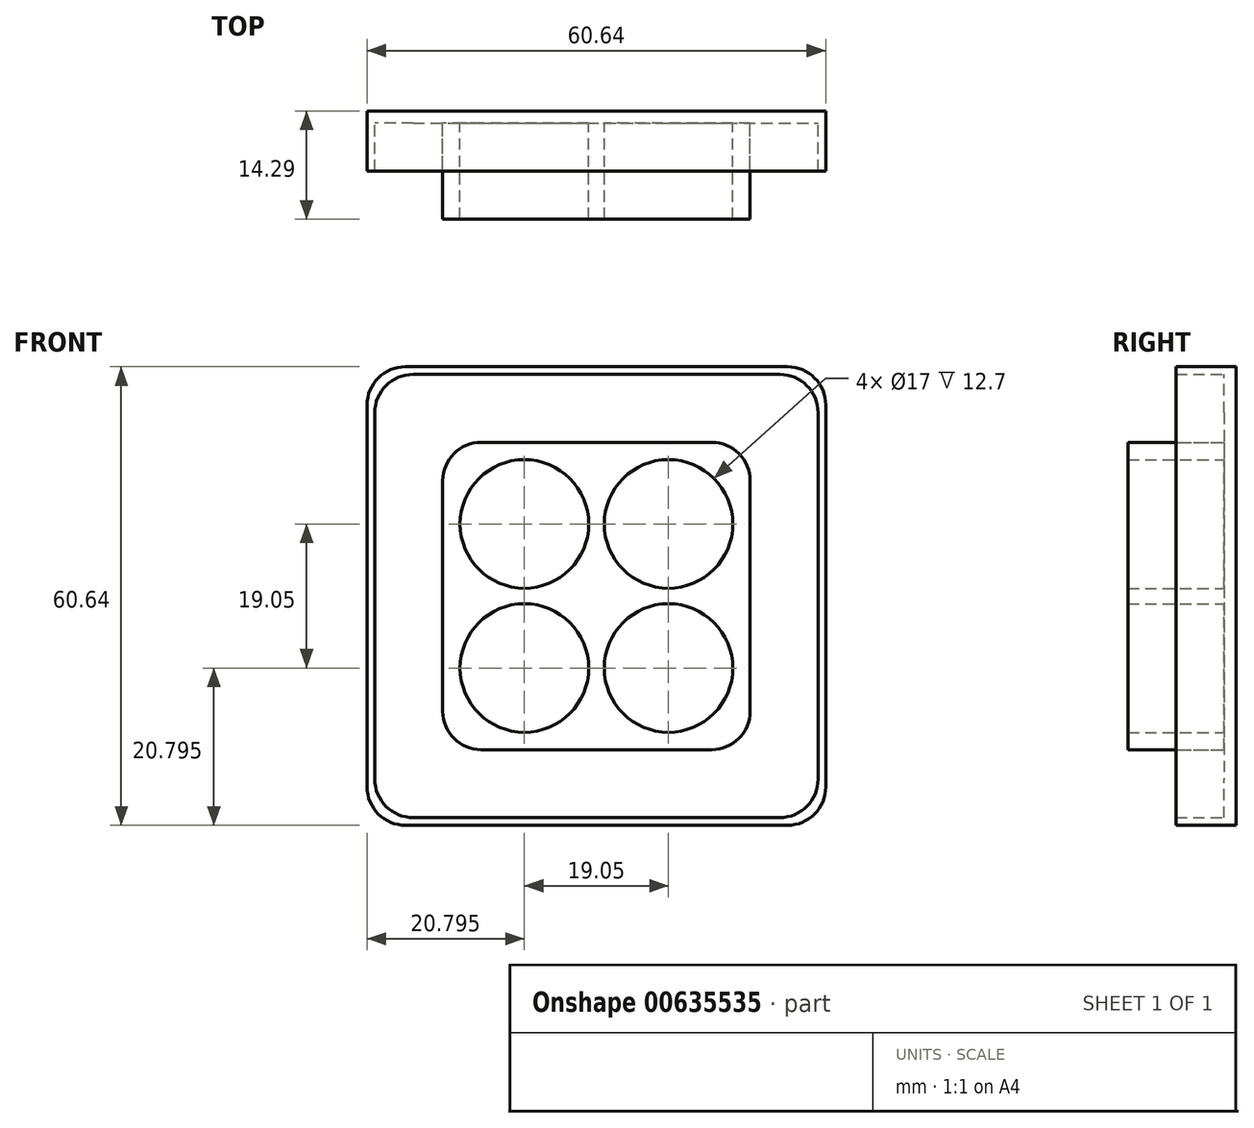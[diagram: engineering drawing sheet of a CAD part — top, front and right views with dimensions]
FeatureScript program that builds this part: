
annotation { "Feature Type Name" : "Feature", "Feature Type Description" : "" }
export const myFeature = defineFeature(function(context is Context, id is Id, definition is map)
    precondition{}
    {
        {
            var Q0;
            Q0=qCreatedBy(makeId("Front.planeOp"),FACE);
            var sketch = newSketch(context, id + "F0", { "sketchPlane" : qUnion([Q0])});
            skLineSegment(sketch, "E0.bottom", {"start": v(-35.56, 40.64) * mm, "end": v(-5.08, 40.64) * mm});
            skLineSegment(sketch, "E0.top", {"start": v(-35.56, 0) * mm, "end": v(-5.08, 0) * mm});
            skLineSegment(sketch, "E0.left", {"start": v(-40.64, 35.56) * mm, "end": v(-40.64, 5.08) * mm});
            skLineSegment(sketch, "E0.right", {"start": v(0, 35.56) * mm, "end": v(0, 5.08) * mm});
            skCircle(sketch, "E1", {"center": v(-29.85, 29.85) * mm, "radius": 8.5 * mm});
            skCircle(sketch, "E2", {"center": v(-10.8, 29.85) * mm, "radius": 8.5 * mm});
            skCircle(sketch, "E3", {"center": v(-29.85, 10.8) * mm, "radius": 8.5 * mm});
            skCircle(sketch, "E4", {"center": v(-10.8, 10.8) * mm, "radius": 8.5 * mm});
            skPoint(sketch, "E5.visualSharp", {"position": v(-40.64, 40.64) * mm});
            skArc(sketch, "E5.filletArc", {"start": v(-35.56, 40.64) * mm, "mid": v(-39.15, 39.15) * mm, "end": v(-40.64, 35.56) * mm});
            skPoint(sketch, "E6.visualSharp", {"position": v(-40.64, 0) * mm});
            skArc(sketch, "E6.filletArc", {"start": v(-40.64, 5.08) * mm, "mid": v(-39.15, 1.49) * mm, "end": v(-35.56, 0) * mm});
            skPoint(sketch, "E7.visualSharp", {"position": v(0, 0) * mm});
            skArc(sketch, "E7.filletArc", {"start": v(-5.08, 0) * mm, "mid": v(-1.49, 1.49) * mm, "end": v(0, 5.08) * mm});
            skPoint(sketch, "E8.visualSharp", {"position": v(0, 40.64) * mm});
            skArc(sketch, "E8.filletArc", {"start": v(0, 35.56) * mm, "mid": v(-1.49, 39.15) * mm, "end": v(-5.08, 40.64) * mm});
            skLineSegment(sketch, "E9.bottom", {"start": v(-45.56, 50.64) * mm, "end": v(4.92, 50.64) * mm});
            skLineSegment(sketch, "E9.top", {"start": v(-45.56, -10) * mm, "end": v(4.92, -10) * mm});
            skLineSegment(sketch, "E9.left", {"start": v(-50.64, 45.56) * mm, "end": v(-50.64, -4.92) * mm});
            skLineSegment(sketch, "E9.right", {"start": v(10, 45.56) * mm, "end": v(10, -4.92) * mm});
            skLineSegment(sketch, "E10.bottom", {"start": v(-10.8, 40.64) * mm, "end": v(-10.8, 40.64) * mm});
            skLineSegment(sketch, "E10.top", {"start": v(-10.8, 50.64) * mm, "end": v(-10.8, 50.64) * mm});
            skPoint(sketch, "E11.visualSharp", {"position": v(-50.64, 50.64) * mm});
            skArc(sketch, "E11.filletArc", {"start": v(-45.56, 50.64) * mm, "mid": v(-49.15, 49.15) * mm, "end": v(-50.64, 45.56) * mm});
            skPoint(sketch, "E12.visualSharp", {"position": v(10, -10) * mm});
            skArc(sketch, "E12.filletArc", {"start": v(4.92, -10) * mm, "mid": v(8.51, -8.51) * mm, "end": v(10, -4.92) * mm});
            skPoint(sketch, "E13.visualSharp", {"position": v(10, 50.64) * mm});
            skArc(sketch, "E13.filletArc", {"start": v(10, 45.56) * mm, "mid": v(8.51, 49.15) * mm, "end": v(4.92, 50.64) * mm});
            skPoint(sketch, "E14.visualSharp", {"position": v(-50.64, -10) * mm});
            skArc(sketch, "E14.filletArc", {"start": v(-50.64, -4.92) * mm, "mid": v(-49.15, -8.51) * mm, "end": v(-45.56, -10) * mm});
            skLineSegment(sketch, "E15.bottom", {"start": v(-44.54, 49.62) * mm, "end": v(3.9, 49.62) * mm});
            skLineSegment(sketch, "E15.top", {"start": v(-44.54, -8.98) * mm, "end": v(3.9, -8.98) * mm});
            skLineSegment(sketch, "E15.left", {"start": v(-49.62, 44.54) * mm, "end": v(-49.62, -3.9) * mm});
            skLineSegment(sketch, "E15.right", {"start": v(8.98, 44.54) * mm, "end": v(8.98, -3.9) * mm});
            skPoint(sketch, "E16.visualSharp", {"position": v(8.98, 49.62) * mm});
            skArc(sketch, "E16.filletArc", {"start": v(8.98, 44.54) * mm, "mid": v(7.5, 48.14) * mm, "end": v(3.9, 49.62) * mm});
            skPoint(sketch, "E17.visualSharp", {"position": v(8.98, -8.98) * mm});
            skArc(sketch, "E17.filletArc", {"start": v(3.9, -8.98) * mm, "mid": v(7.5, -7.5) * mm, "end": v(8.98, -3.9) * mm});
            skPoint(sketch, "E18.visualSharp", {"position": v(-49.62, -8.98) * mm});
            skArc(sketch, "E18.filletArc", {"start": v(-49.62, -3.9) * mm, "mid": v(-48.14, -7.5) * mm, "end": v(-44.54, -8.98) * mm});
            skPoint(sketch, "E19.visualSharp", {"position": v(-49.62, 49.62) * mm});
            skArc(sketch, "E19.filletArc", {"start": v(-44.54, 49.62) * mm, "mid": v(-48.14, 48.14) * mm, "end": v(-49.62, 44.54) * mm});
            skSolve(sketch);
        }
        {
            var Q0;
            Q0 = qSketchRegion(id + "F0", true);
            var Q1;
            Q1=makeQuery(id+"F0.imprint","IMPRINT",FACE,{"disambiguationData":[TD([[makeQuery(id+"F0.imprint","IMPRINT",EDGE,{"derivedFrom":sQuery(id+"F0.wireOp",EDGE,"E2")}),1.0]])]});
            var Q2;
            Q2=makeQuery(id+"F0.imprint","IMPRINT",FACE,{"disambiguationData":[TD([[makeQuery(id+"F0.imprint","IMPRINT",EDGE,{"derivedFrom":sQuery(id+"F0.wireOp",EDGE,"E1")}),1.0]])]});
            var Q3;
            Q3=makeQuery(id+"F0.imprint","IMPRINT",FACE,{"disambiguationData":[TD([[makeQuery(id+"F0.imprint","IMPRINT",EDGE,{"derivedFrom":sQuery(id+"F0.wireOp",EDGE,"E3")}),1.0]])]});
            var Q4;
            Q4=makeQuery(id+"F0.imprint","IMPRINT",FACE,{"disambiguationData":[TD([[makeQuery(id+"F0.imprint","IMPRINT",EDGE,{"derivedFrom":sQuery(id+"F0.wireOp",EDGE,"E4")}),1.0]])]});
            var Q5;
            Q5=makeQuery(id+"F0.imprint","IMPRINT",FACE,{"disambiguationData":[TD([[makeQuery(id+"F0.imprint","IMPRINT",EDGE,{"derivedFrom":sQuery(id+"F0.wireOp",EDGE,"E0.bottom")}),-1.0]])]});
            var Q6;
            Q6=makeQuery(id+"F0.imprint","IMPRINT",FACE,{"disambiguationData":[TD([[makeQuery(id+"F0.imprint","IMPRINT",EDGE,{"derivedFrom":sQuery(id+"F0.wireOp",EDGE,"E0.bottom")}),1.0]])]});
            extrude(context, id + "F1", {"entities" : qUnion([Q0, Q1, Q2, Q3, Q4, Q5, Q6]), "oppositeDirection" : true, "depth" : 1.59 * mm, "offsetDistance" : 25.4 * mm});
        }
        {
            var Q0;
            Q0=makeQuery(id+"F0.imprint","IMPRINT",FACE,{"disambiguationData":[TD([[makeQuery(id+"F0.imprint","IMPRINT",EDGE,{"derivedFrom":sQuery(id+"F0.wireOp",EDGE,"E0.bottom")}),-1.0]])]});
            extrude(context, id + "F2", {"entities" : qUnion([Q0]), "operationType" : NewBodyOperationType.ADD, "depth" : 12.7 * mm, "offsetDistance" : 25.4 * mm});
        }
        {
            var Q0;
            Q0=makeQuery(id+"F0.imprint","IMPRINT",FACE,{"disambiguationData":[TD([[makeQuery(id+"F0.imprint","IMPRINT",EDGE,{"derivedFrom":sQuery(id+"F0.wireOp",EDGE,"E9.bottom")}),-1.0]])]});
            extrude(context, id + "F3", {"entities" : qUnion([Q0]), "operationType" : NewBodyOperationType.ADD, "depth" : 6.35 * mm, "offsetDistance" : 25.4 * mm});
        }
    });
